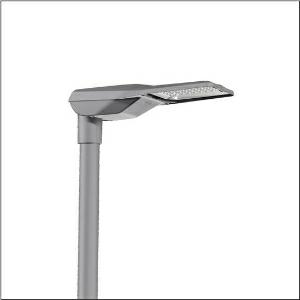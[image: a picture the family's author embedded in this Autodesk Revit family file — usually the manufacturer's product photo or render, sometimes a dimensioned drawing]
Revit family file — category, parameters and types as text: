
# Revit family: streetlight_sl_21_iq_mini___p1_0a_5xe2a41d08gb_135c
name_source: partatom
category: Lighting Fixtures
units: mm (PartAtom-declared; Revit-internal decimal feet)

## family parameters
Cut with Voids When Loaded = No
Host = Face
Light Source = No
Part Type = Normal
Room Calculation Point = No
Round Connector Dimension = Use Diameter
Shared = No

## types (1)
- --- (1 x LED, 5920 lm, 37.1 W, 4000K)
    Apparent Load = 37 VA
    CIE Flux Codes = 21 50 90 100 100
    Color Rendering = 70
    Color Temperature = 4000K
    Default Elevation = 1800 mm
    Description = Streetlight SL 21 iQ mini, mast luminaire, primary light control with lens, of PMMA, primary optical cover: cover, of toughened safety glass, transparent, light distribution: P1.0a, light emission: direct distribution, primary light characteristic: asymmetric, installation type: post-top, side-entry, LED, High Power LED, rated luminous flux: 5.920lm, luminous efficacy: 160lm/W, light colour: 740, colour temperature: 4000K, control gear: iQ-Comfort, control: Auto-Match, Temp-Guard, Lumen-Switch, Night-Set, Smart-Wire, Light-Fading, Desk-Remote (wireless, voltage-free reading and setting of iQ features in the workshop via application-optimized NFC function/RFID function), optimised constant luminous flux control (CLO 2.0), pre-setting: linear dimming characteristic, mains connection: 220..240V, AC, 50/60Hz, start of lifetime: 37W, end of service life: 39W, reduction: 18W, luminaire housing, of diecast aluminium, powder-coated, Siteco® metallic grey (DB 702S), corrosivity category C5 mid according to DIN EN ISO 12944, please order mast flange separately, inclination adjustable: 0°, 5°, 10°, 15°, sealing non-destructively replaceable, multi-level sealing system, length: 628mm, width: 235mm, height: 110mm, mast flange for spigot size: 42mm (side-entry): 5XC10008XM4, 60/48mm (side-entry/post-top): 5XC10108XM2, 76/60mm (side-entry/post-top): 5XC10108XM1, mounting height: 4..8m, protection rating (complete): IP66, insulation class (complete): insulation class II (safety insulation), certification: CE, ENEC, ENEC+, VDE, impact resistance: IK10, permissible operating ambient temperature for outdoor applications: -40..+50°C, standard-compliant lighting for roads and squares, packaging unit: 1 piece

Light Distribution: P1.0a
    Height = 110 mm
    Lamp = 1 x LED
    Lamp Light Flux = 5920 lm
    Lamp Power = 37.1 W
    Lamp count = 1
    Length = 625 mm
    Luminous efficacy = 160 lm/W
    Manufacturer = Siteco
    ModVariant = No
    Model = 5XE2A41D08GB
    Number of Poles = 1
    OnlyDefault = Yes
    Power Factor = 1
    Product Name = Streetlight SL 21 iQ mini | P1.0a
    Product group = mast luminaire | pylon top
    ProductGroupID = 6100
    Protection Class = Protection class II
    Protection Degree = IP 66
    RLX_Detail_Level = 1
    RLX_Emergency_Light_Flux = 0 lm
    RLX_Emergency_Type = 0
    RLX_Emergency_Type_DB = No
    RlxData = <blob elided: 37565 chars, md5=1d5ceab7>
    Socket = socket
    Standby Power = 0 W
    System Light Flux = 5920 lm
    System Power = 37 W
    Type Comments = factory setting: luminous flux: 100 % | dim-lin: 254 | 385 mA
    Type Image = l_1003519.jpg
    URL = http://relux.com
    VarID = @adj_186776
    Voltage = 0 V
    Weight = 0.00 kg
    Width = 234 mm

## geometry (parser evidence)
native form markers: Blend x4, Sweep x10
no freeform markers — native parametric forms only
